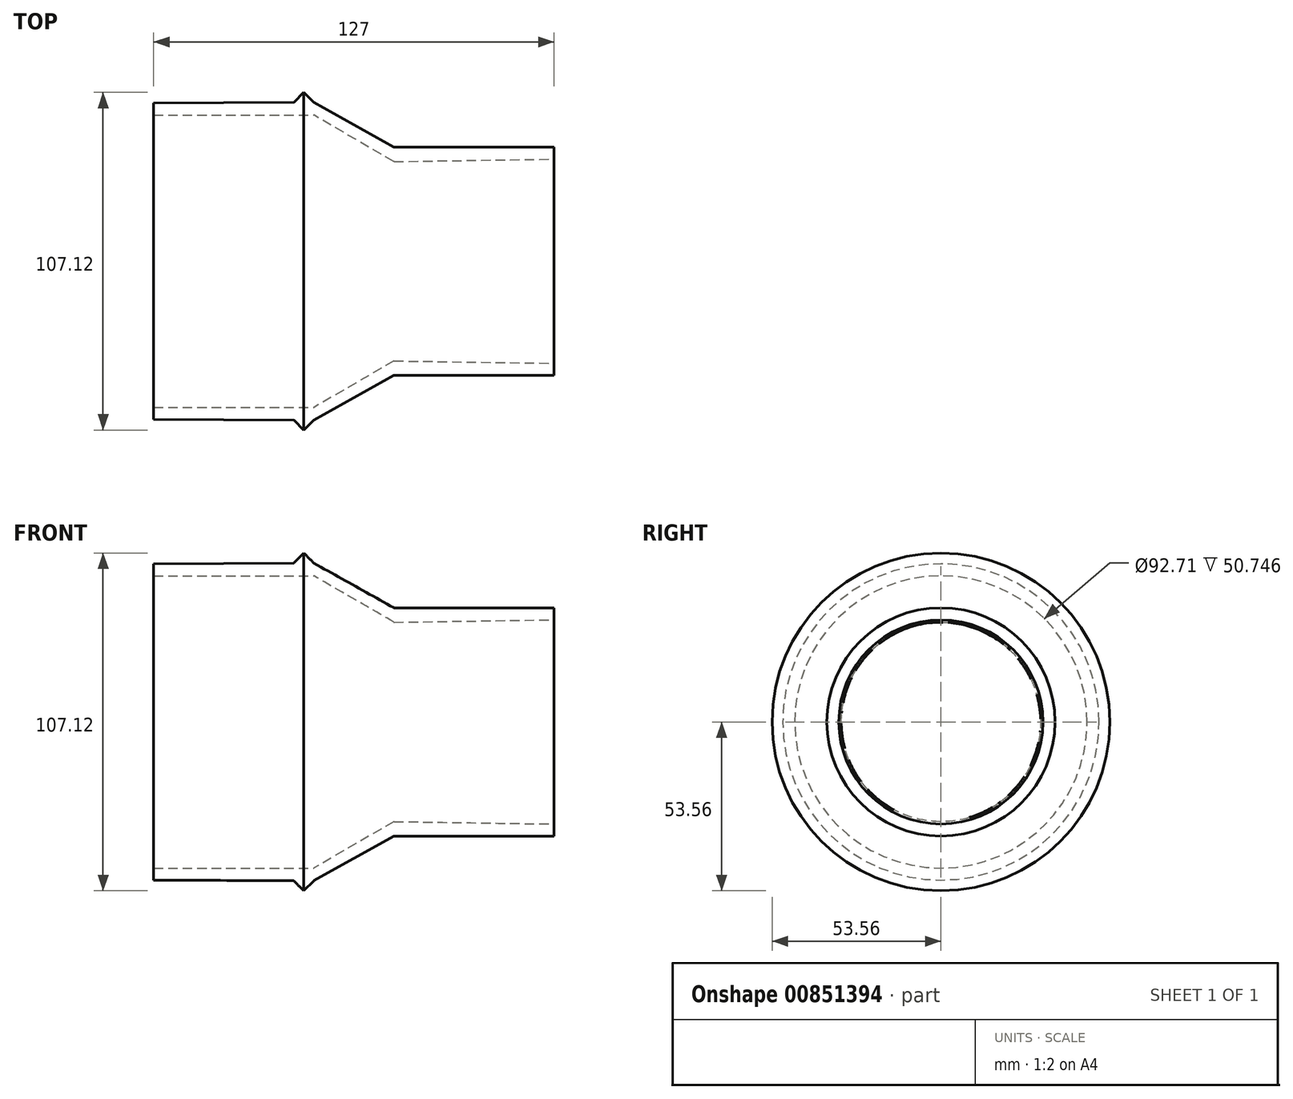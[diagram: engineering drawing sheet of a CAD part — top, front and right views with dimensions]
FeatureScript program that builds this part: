
annotation { "Feature Type Name" : "Feature", "Feature Type Description" : "" }
export const myFeature = defineFeature(function(context is Context, id is Id, definition is map)
    precondition{}
    {
        {
            assignVariable(context, id + "F0", {"name" : "fillet", "anyValue" : .2});
        }
        {
            var Q0;
            Q0=qCreatedBy(makeId("Front.planeOp"),FACE);
            var sketch = newSketch(context, id + "F1", { "sketchPlane" : qUnion([Q0])});
            skLineSegment(sketch, "E0", {"start": v(0, 0) * mm, "end": v(-48.8, 0) * mm, "construction": true});
            skLineSegment(sketch, "E1", {"start": v(0, 31.62) * mm, "end": v(50.8, 32.39) * mm});
            skLineSegment(sketch, "E2", {"start": v(50.8, 32.39) * mm, "end": v(50.8, 36.2) * mm});
            skLineSegment(sketch, "E3", {"start": v(50.8, 36.2) * mm, "end": v(0, 36.2) * mm});
            skPoint(sketch, "E4", {"position": v(8.9, 31.75) * mm});
            skLineSegment(sketch, "E5", {"start": v(0, 36.2) * mm, "end": v(-25.4, 50.39) * mm});
            skLineSegment(sketch, "E6", {"start": v(-25.4, 50.39) * mm, "end": v(-28.57, 53.56) * mm});
            skLineSegment(sketch, "E7", {"start": v(-28.58, 53.56) * mm, "end": v(-31.75, 50.39) * mm});
            skLineSegment(sketch, "E8", {"start": v(-31.75, 50.39) * mm, "end": v(-76.2, 50.16) * mm});
            skLineSegment(sketch, "E9", {"start": v(-76.2, 50.16) * mm, "end": v(-76.2, 46.35) * mm});
            skLineSegment(sketch, "E10", {"start": v(-76.2, 46.35) * mm, "end": v(-25.4, 46.36) * mm});
            skLineSegment(sketch, "E11", {"start": v(-25.4, 46.36) * mm, "end": v(0, 31.62) * mm});
            skLineSegment(sketch, "E12", {"start": v(-31.75, 50.39) * mm, "end": v(-25.4, 50.39) * mm, "construction": true});
            skLineSegment(sketch, "E13", {"start": v(-25.4, 50.39) * mm, "end": v(-25.4, 46.36) * mm, "construction": true});
            skLineSegment(sketch, "E14", {"start": v(-28.58, 50.39) * mm, "end": v(-28.58, 53.56) * mm, "construction": true});
            skPoint(sketch, "E15", {"position": v(-50.8, 50.3) * mm});
            skSolve(sketch);
        }
        {
            var Q0;
            Q0=qSketchRegion(id+"F1",true);
            var Q1;
            Q1=sQuery(id+"F1.wireOp",EDGE,"E0");
            revolve(context, id + "F2", {"surfaceOperationType" : NewSurfaceOperationType.NEW, "entities" : qUnion([Q0]), "axis" : qUnion([Q1]), "revolveType" : RevolveType.FULL});
        }
        {
            var Q0;
            Q0=makeQuery(id+"F2.opRevolve","SWEPT_EDGE",EDGE,{"disambiguationData":[OSD([sQuery(id+"F1.wireOp",EDGE,"E10"),sQuery(id+"F1.wireOp",EDGE,"E11")])]});
            var Q1;
            Q1=makeQuery(id+"F2.opRevolve","SWEPT_EDGE",EDGE,{"disambiguationData":[OSD([sQuery(id+"F1.wireOp",EDGE,"E1"),sQuery(id+"F1.wireOp",EDGE,"E11")])]});
            var Q2;
            Q2=makeQuery(id+"F2.opRevolve","SWEPT_EDGE",EDGE,{"disambiguationData":[OSD([sQuery(id+"F1.wireOp",EDGE,"E3"),sQuery(id+"F1.wireOp",EDGE,"E5")])]});
            var Q3;
            Q3=makeQuery(id+"F2.opRevolve","SWEPT_EDGE",EDGE,{"disambiguationData":[OSD([sQuery(id+"F1.wireOp",EDGE,"E7"),sQuery(id+"F1.wireOp",EDGE,"E8")])]});
            var Q4;
            Q4=makeQuery(id+"F2.opRevolve","SWEPT_EDGE",EDGE,{"disambiguationData":[OSD([sQuery(id+"F1.wireOp",EDGE,"E5"),sQuery(id+"F1.wireOp",EDGE,"E6")])]});
            fillet(context, id + "F3", {"entities" : qUnion([Q0, Q1, Q2, Q3, Q4]), "radius" : (getVariable(context, 'fillet')) * mm, "tangentPropagation" : true, "allowEdgeOverflow" : false});
        }
    });
